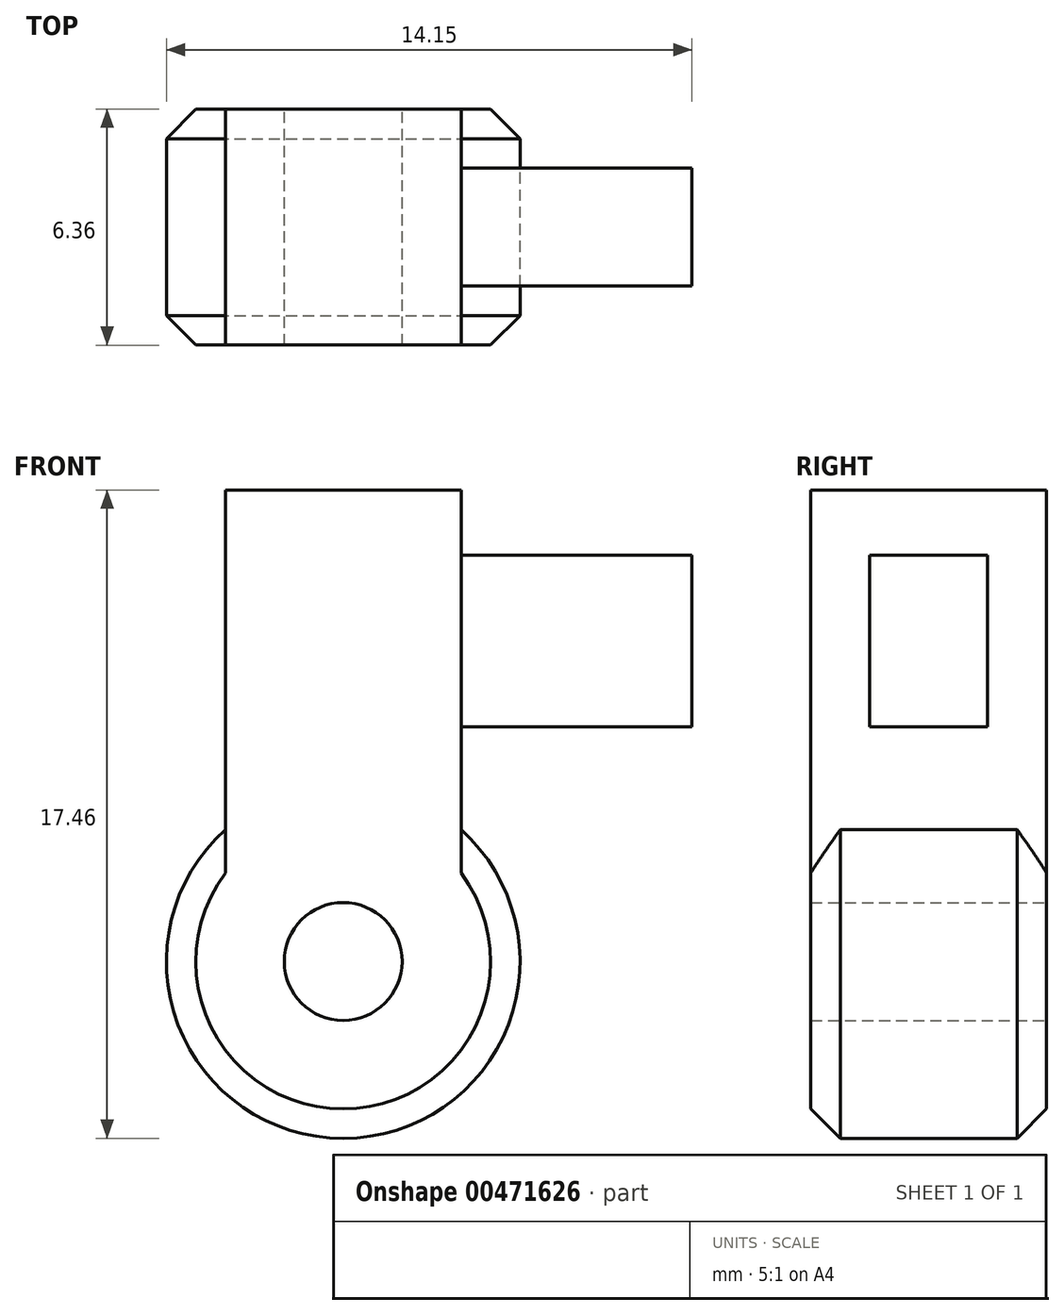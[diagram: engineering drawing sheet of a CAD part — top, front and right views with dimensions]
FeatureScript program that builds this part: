
annotation { "Feature Type Name" : "Feature", "Feature Type Description" : "" }
export const myFeature = defineFeature(function(context is Context, id is Id, definition is map)
    precondition{}
    {
        {
            var Q0;
            Q0=qCreatedBy(makeId("Front.planeOp"),FACE);
            var sketch = newSketch(context, id + "F0", { "sketchPlane" : qUnion([Q0])});
            skCircle(sketch, "E0", {"center": v(0, 0) * mm, "radius": 1.59 * mm});
            skCircle(sketch, "E1.0", {"center": v(0, 0) * mm, "radius": 4.76 * mm});
            skSolve(sketch);
        }
        {
            var Q0;
            Q0=qCreatedBy(makeId("Front.planeOp"),FACE);
            var sketch = newSketch(context, id + "F1", { "sketchPlane" : qUnion([Q0])});
            skLineSegment(sketch, "E2.bottom", {"start": v(3.18, 12.7) * mm, "end": v(-3.17, 12.7) * mm});
            skLineSegment(sketch, "E2.left", {"start": v(3.18, 12.7) * mm, "end": v(3.18, 0) * mm});
            skLineSegment(sketch, "E2.right", {"start": v(-3.17, 12.7) * mm, "end": v(-3.18, 0) * mm});
            skPoint(sketch, "E2.middle", {"position": v(0, 0) * mm});
            skPoint(sketch, "E3", {"position": v(3.18, 0) * mm});
            skPoint(sketch, "E4", {"position": v(-3.18, 0) * mm});
            skLineSegment(sketch, "E5", {"start": v(3.18, 0) * mm, "end": v(-3.18, 0) * mm});
            skSolve(sketch);
        }
        {
            var Q0;
            Q0=qCreatedBy(makeId("Front.planeOp"),FACE);
            var sketch = newSketch(context, id + "F2", { "sketchPlane" : qUnion([Q0])});
            skLineSegment(sketch, "E6.bottom", {"start": v(9.4, 6.32) * mm, "end": v(2.1, 6.32) * mm});
            skLineSegment(sketch, "E6.top", {"start": v(9.4, 10.94) * mm, "end": v(2.1, 10.94) * mm});
            skLineSegment(sketch, "E6.left", {"start": v(9.4, 6.32) * mm, "end": v(9.4, 10.94) * mm});
            skLineSegment(sketch, "E6.right", {"start": v(2.1, 6.32) * mm, "end": v(2.1, 10.94) * mm});
            skSolve(sketch);
        }
        {
            var Q0;
            Q0=qCreatedBy(makeId("Front.planeOp"),FACE);
            var sketch = newSketch(context, id + "F3", { "sketchPlane" : qUnion([Q0])});
            skCircle(sketch, "E7", {"center": v(0, 0) * mm, "radius": 1.59 * mm});
            skSolve(sketch);
        }
        {
            var Q0;
            Q0=makeQuery(id+"F0.imprint","IMPRINT",FACE,{"disambiguationData":[TD([[makeQuery(id+"F0.imprint","IMPRINT",EDGE,{"derivedFrom":sQuery(id+"F0.wireOp",EDGE,"E0")}),-1.0]])]});
            extrude(context, id + "F4", {"entities" : qUnion([Q0]), "depth" : 6.35 * mm, "symmetric" : true});
        }
        {
            var Q0;
            Q0=makeQuery(id+"F1.imprint","IMPRINT",FACE,{"disambiguationData":[TD([[makeQuery(id+"F1.imprint","IMPRINT",EDGE,{"derivedFrom":sQuery(id+"F1.wireOp",EDGE,"E2.bottom")}),1.0]])]});
            extrude(context, id + "F5", {"entities" : qUnion([Q0]), "operationType" : NewBodyOperationType.ADD, "depth" : 6.35 * mm, "symmetric" : true});
        }
        {
            var Q0;
            Q0 = qSketchRegion(id + "F3", true);
            extrude(context, id + "F6", {"entities" : qUnion([Q0]), "operationType" : NewBodyOperationType.REMOVE, "oppositeDirection" : true, "depth" : 25.4 * mm, "symmetric" : true});
        }
        {
            var Q0;
            Q0=makeQuery(id+"F4.opExtrude","CAP_EDGE",EDGE,{"disambiguationData":[OSD([sQuery(id+"F0.wireOp",EDGE,"E1.0")])],"isStart":true});
            var Q1;
            Q1=makeQuery(id+"F4.opExtrude","CAP_EDGE",EDGE,{"disambiguationData":[OSD([sQuery(id+"F0.wireOp",EDGE,"E1.0")])],"isStart":false});
            chamfer(context, id + "F7", {"entities" : qUnion([Q0, Q1]), "width" : 0.8 * mm, "tangentPropagation" : true});
        }
        {
            var Q0;
            Q0=makeQuery(id+"F2.imprint","IMPRINT",FACE,{"disambiguationData":[TD([[makeQuery(id+"F2.imprint","IMPRINT",EDGE,{"derivedFrom":sQuery(id+"F2.wireOp",EDGE,"E6.bottom")}),-1.0]])]});
            extrude(context, id + "F8", {"entities" : qUnion([Q0]), "operationType" : NewBodyOperationType.ADD, "depth" : 3.17 * mm, "symmetric" : true});
        }
    });
